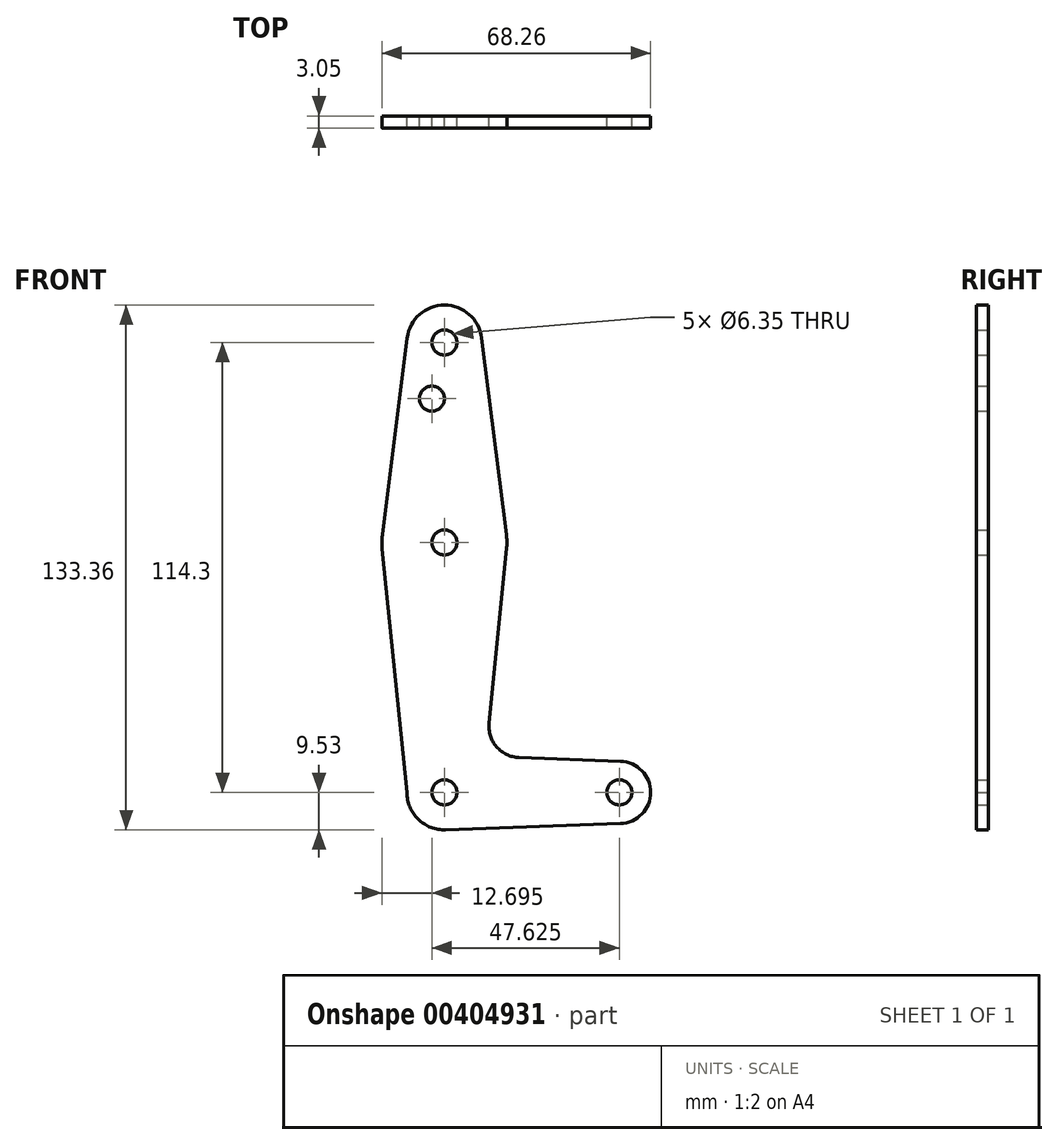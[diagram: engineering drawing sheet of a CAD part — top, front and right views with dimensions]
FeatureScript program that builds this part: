
annotation { "Feature Type Name" : "Feature", "Feature Type Description" : "" }
export const myFeature = defineFeature(function(context is Context, id is Id, definition is map)
    precondition{}
    {
        {
            var Q0;
            Q0=qCreatedBy(makeId("Front.planeOp"),FACE);
            var sketch = newSketch(context, id + "F0", { "sketchPlane" : qUnion([Q0])});
            skCircle(sketch, "E0", {"center": v(0, 0) * mm, "radius": 9.53 * mm});
            skCircle(sketch, "E1", {"center": v(44.45, 0) * mm, "radius": 7.94 * mm});
            skCircle(sketch, "E2", {"center": v(0, 63.5) * mm, "radius": 15.88 * mm});
            skCircle(sketch, "E3", {"center": v(0, 114.3) * mm, "radius": 9.53 * mm});
            skLineSegment(sketch, "E4", {"start": v(0, 0) * mm, "end": v(44.45, 0) * mm, "construction": true});
            skLineSegment(sketch, "E5", {"start": v(0, 0) * mm, "end": v(0, 114.3) * mm, "construction": true});
            skLineSegment(sketch, "E6", {"start": v(-9.52, 0) * mm, "end": v(-15.8, 61.9) * mm});
            skLineSegment(sketch, "E7", {"start": v(-15.75, 65.48) * mm, "end": v(-9.45, 115.5) * mm});
            skLineSegment(sketch, "E8", {"start": v(9.45, 115.5) * mm, "end": v(15.75, 65.48) * mm});
            skLineSegment(sketch, "E9", {"start": v(11.34, 17.6) * mm, "end": v(15.8, 61.91) * mm});
            skLineSegment(sketch, "E10", {"start": v(18.97, 8.85) * mm, "end": v(44.73, 7.93) * mm});
            skLineSegment(sketch, "E11", {"start": v(0.34, -9.52) * mm, "end": v(44.73, -7.93) * mm});
            skCircle(sketch, "E12", {"center": v(0, 0) * mm, "radius": 3.18 * mm});
            skCircle(sketch, "E13", {"center": v(44.45, 0) * mm, "radius": 3.18 * mm});
            skCircle(sketch, "E14", {"center": v(0, 63.5) * mm, "radius": 3.18 * mm});
            skCircle(sketch, "E15", {"center": v(0, 114.3) * mm, "radius": 3.18 * mm});
            skCircle(sketch, "E16", {"center": v(-3.18, 100.03) * mm, "radius": 3.18 * mm});
            skArc(sketch, "E17.filletArc", {"start": v(11.34, 17.6) * mm, "mid": v(13.26, 11.57) * mm, "end": v(18.97, 8.85) * mm});
            skSolve(sketch);
        }
        {
            var Q0;
            Q0 = qSketchRegion(id + "F0", true);
            extrude(context, id + "F1", {"entities" : qUnion([Q0]), "depth" : 3.05 * mm});
        }
    });
